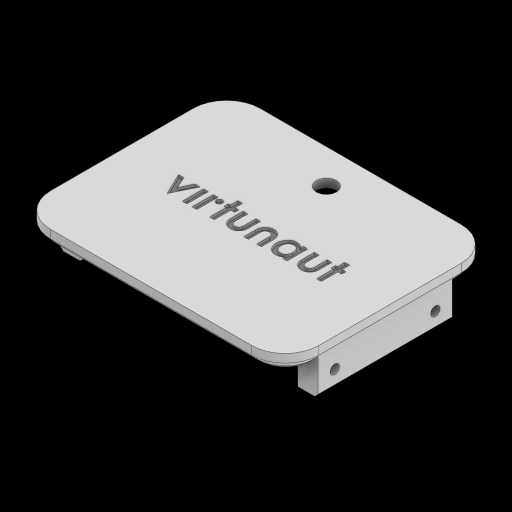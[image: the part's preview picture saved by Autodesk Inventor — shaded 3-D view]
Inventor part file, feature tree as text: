
AUTODESK INVENTOR PART (.ipt)
format: ipt  version: 2024 (Build 280153000, 153)  size: 8,517,632 bytes
history: native  units: mm
features: sketch x10, extrude x7, chamfer x3, projected_geometry x2, fillet x1, hole x1, other x1
ambient origin geometry x8: Origin, YZ Plane, XZ Plane, XY Plane, X Axis, Y Axis, Z Axis, Center Point
bodies: Volumenkörper1 (feature_tree)
feature tree (25):
  extrude  "Extrusion1"  Depth=125.0mm
  fillet  "Rundung1"  Radius=5.0mm
  extrude  "Extrusion3"  Depth=20.0mm
  extrude  "Extrusion4"  Depth=30.0mm
  hole  "Bohrung1"  [1 undecoded]
  chamfer  "Fasen1"  Distance=4.0mm
  sketch  "Skizze7"  dims[d36=8.0mm]
  extrude  "Extrusion6"  Depth=7.0mm TaperAngle=0.0deg
  sketch  "Skizze9"  dims[d38=8.0mm]
  extrude  "Extrusion7"  Depth=3.0mm
  extrude  "Extrusion8"  Depth=80.0mm
  extrude  "Extrusion9"  Depth=2.0mm
  chamfer  "Fasen2"  Distance=12.0mm
  chamfer  "Fasen3"  Distance=3.0mm
  sketch  "Skizze1"  dims[d0=160.0mm d1=125.0mm d2=5.0mm d3=0.0mm]
  sketch  "Skizze3"  dims[d4=20.0mm d31=13.0mm]
  sketch  "Skizze4"  dims[d32=30.0mm d33=8.0mm]
  sketch  "Skizze5"  dims[d34=75.5mm d35=95.0mm]
  projected_geometry  "Projizierte Kontur1"
  other  "Bild2"
  sketch  "Skizze8"  dims[d37=8.0mm]
  sketch  "Skizze10"  dims[d39=4.0mm]
  sketch  "Skizze11"  dims[d40=4.0mm]
  sketch  "Skizze12"  dims[d41=4.0mm d42=4.0mm d43=7.0mm d44=0.0mm d45=3.0mm d46=80.0mm d47=40.0mm d48=12.0mm d49=3.0mm d50=12.0mm d51=80.0mm d52=40.0mm d53=25.0mm d54=0.0mm d55=30.0mm d56=30.0mm d57=15.0mm d58=15.0mm d59=5.6mm d60=6.0mm d61=9.4mm d62=2.0mm d63=90.0deg d64=8.0mm d65=20.594885mm d66=2.0mm d67=2.0mm d68=45.0deg d74=100.0mm d84=17.505211mm d85=8.752605mm d86=50.0mm d88=100.0mm d90=1.5mm d91=0.0mm d93=1.5mm d94=0.0mm d95=12.0mm d97=10.0mm d98=0.0mm d100=3.0mm d101=3.0mm d102=35.0mm d103=5.0mm d104=0.0mm d105=5.0mm d106=2.0mm d107=45.0deg d108=1.5mm d109=2.0mm d110=45.0deg d111=42.0mm]
  projected_geometry  "Projizierte Kontur2"
note: 1 required parameter value undecoded (feature->parameter linkage not recoverable at this tier; creation-order binding heuristic only, values carry confidence <= 0.55)
